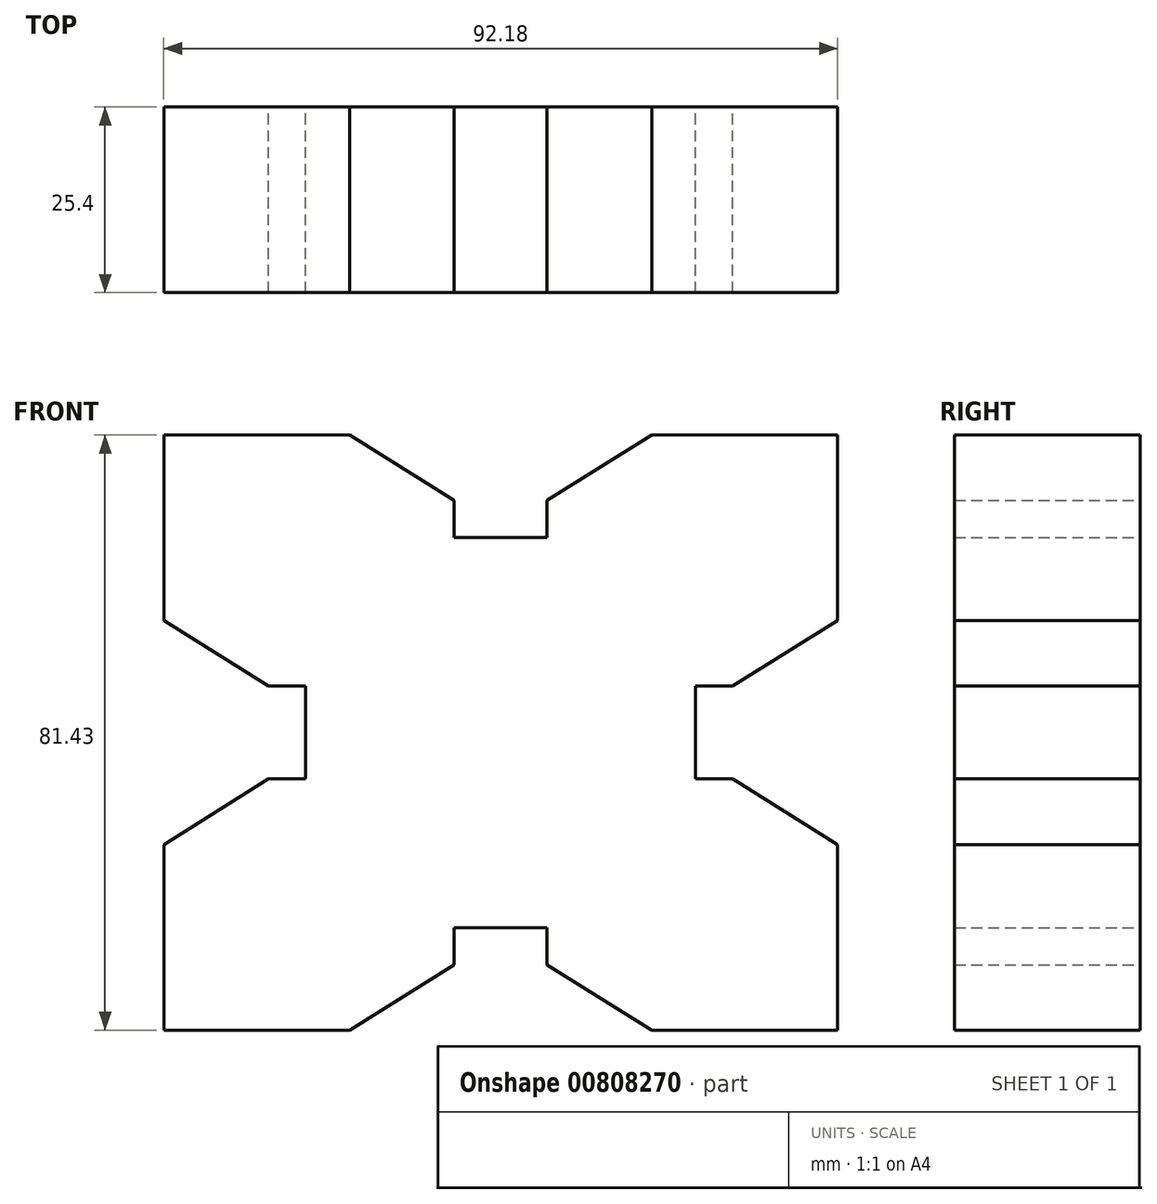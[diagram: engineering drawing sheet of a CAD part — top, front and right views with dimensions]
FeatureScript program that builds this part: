
annotation { "Feature Type Name" : "Feature", "Feature Type Description" : "" }
export const myFeature = defineFeature(function(context is Context, id is Id, definition is map)
    precondition{}
    {
        {
            var Q0;
            Q0=qCreatedBy(makeId("Front.planeOp"),FACE);
            var sketch = newSketch(context, id + "F0", { "sketchPlane" : qUnion([Q0])});
            skLineSegment(sketch, "E0", {"start": v(-79.48, 25.4) * mm, "end": v(-79.48, 0) * mm});
            skLineSegment(sketch, "E1", {"start": v(-79.48, 0) * mm, "end": v(-54.08, 0) * mm});
            skLineSegment(sketch, "E2", {"start": v(-12.7, 0) * mm, "end": v(12.7, 0) * mm});
            skLineSegment(sketch, "E3", {"start": v(12.7, 0) * mm, "end": v(12.7, 25.4) * mm});
            skLineSegment(sketch, "E4", {"start": v(-54.08, 0) * mm, "end": v(-39.74, 8.96) * mm});
            skLineSegment(sketch, "E5", {"start": v(-39.74, 8.96) * mm, "end": v(-39.74, 14.04) * mm});
            skLineSegment(sketch, "E6", {"start": v(-39.74, 14.04) * mm, "end": v(-27.04, 14.04) * mm});
            skLineSegment(sketch, "E7", {"start": v(-27.04, 14.04) * mm, "end": v(-27.04, 8.96) * mm});
            skLineSegment(sketch, "E8", {"start": v(-27.04, 8.96) * mm, "end": v(-12.7, 0) * mm});
            skLineSegment(sketch, "E9", {"start": v(12.7, 25.4) * mm, "end": v(-1.65, 34.36) * mm});
            skLineSegment(sketch, "E10", {"start": v(-79.48, 25.4) * mm, "end": v(-65.13, 34.36) * mm});
            skLineSegment(sketch, "E11", {"start": v(-65.13, 34.36) * mm, "end": v(-60.05, 34.36) * mm});
            skLineSegment(sketch, "E12", {"start": v(-60.05, 34.36) * mm, "end": v(-60.05, 40.71) * mm});
            skLineSegment(sketch, "E13", {"start": v(-1.65, 34.36) * mm, "end": v(-6.73, 34.36) * mm});
            skLineSegment(sketch, "E14", {"start": v(-6.73, 34.36) * mm, "end": v(-6.73, 40.71) * mm});
            skLineSegment(sketch, "E15", {"start": v(-60.05, 40.71) * mm, "end": v(-6.73, 40.71) * mm});
            skLineSegment(sketch, "E16.MirrorCS", {"start": v(-60.05, 47.06) * mm, "end": v(-60.05, 40.71) * mm});
            skLineSegment(sketch, "E17.MirrorCS", {"start": v(-65.13, 47.06) * mm, "end": v(-60.05, 47.06) * mm});
            skLineSegment(sketch, "E18.MirrorCS", {"start": v(-79.48, 56.03) * mm, "end": v(-65.13, 47.06) * mm});
            skLineSegment(sketch, "E19.MirrorCS", {"start": v(-79.48, 56.03) * mm, "end": v(-79.48, 81.43) * mm});
            skLineSegment(sketch, "E20.MirrorCS", {"start": v(-79.48, 81.43) * mm, "end": v(-54.08, 81.43) * mm});
            skLineSegment(sketch, "E21.MirrorCS", {"start": v(-54.08, 81.43) * mm, "end": v(-39.74, 72.47) * mm});
            skLineSegment(sketch, "E22.MirrorCS", {"start": v(-39.74, 72.47) * mm, "end": v(-39.74, 67.39) * mm});
            skLineSegment(sketch, "E23.MirrorCS", {"start": v(-39.74, 67.39) * mm, "end": v(-27.04, 67.39) * mm});
            skLineSegment(sketch, "E24.MirrorCS", {"start": v(-27.04, 67.39) * mm, "end": v(-27.04, 72.47) * mm});
            skLineSegment(sketch, "E25.MirrorCS", {"start": v(-27.04, 72.47) * mm, "end": v(-12.7, 81.43) * mm});
            skLineSegment(sketch, "E26.MirrorCS", {"start": v(-12.7, 81.43) * mm, "end": v(12.7, 81.43) * mm});
            skLineSegment(sketch, "E27.MirrorCS", {"start": v(12.7, 81.43) * mm, "end": v(12.7, 56.03) * mm});
            skLineSegment(sketch, "E28.MirrorCS", {"start": v(12.7, 56.03) * mm, "end": v(-1.65, 47.06) * mm});
            skLineSegment(sketch, "E29.MirrorCS", {"start": v(-1.65, 47.06) * mm, "end": v(-6.73, 47.06) * mm});
            skLineSegment(sketch, "E30.MirrorCS", {"start": v(-6.73, 47.06) * mm, "end": v(-6.73, 40.71) * mm});
            skSolve(sketch);
        }
        {
            var Q0;
            Q0=makeQuery(id+"F0.imprint","IMPRINT",FACE,{"disambiguationData":[TD([[makeQuery(id+"F0.imprint","IMPRINT",EDGE,{"derivedFrom":sQuery(id+"F0.wireOp",EDGE,"E15")}),1.0]])]});
            var Q1;
            Q1=makeQuery(id+"F0.imprint","IMPRINT",FACE,{"disambiguationData":[TD([[makeQuery(id+"F0.imprint","IMPRINT",EDGE,{"derivedFrom":sQuery(id+"F0.wireOp",EDGE,"E0")}),1.0]])]});
            extrude(context, id + "F1", {"entities" : qUnion([Q0, Q1]), "endBound" : BoundingType.SYMMETRIC, "depth" : 25.4 * mm, "offsetDistance" : 25.4 * mm});
        }
    });
